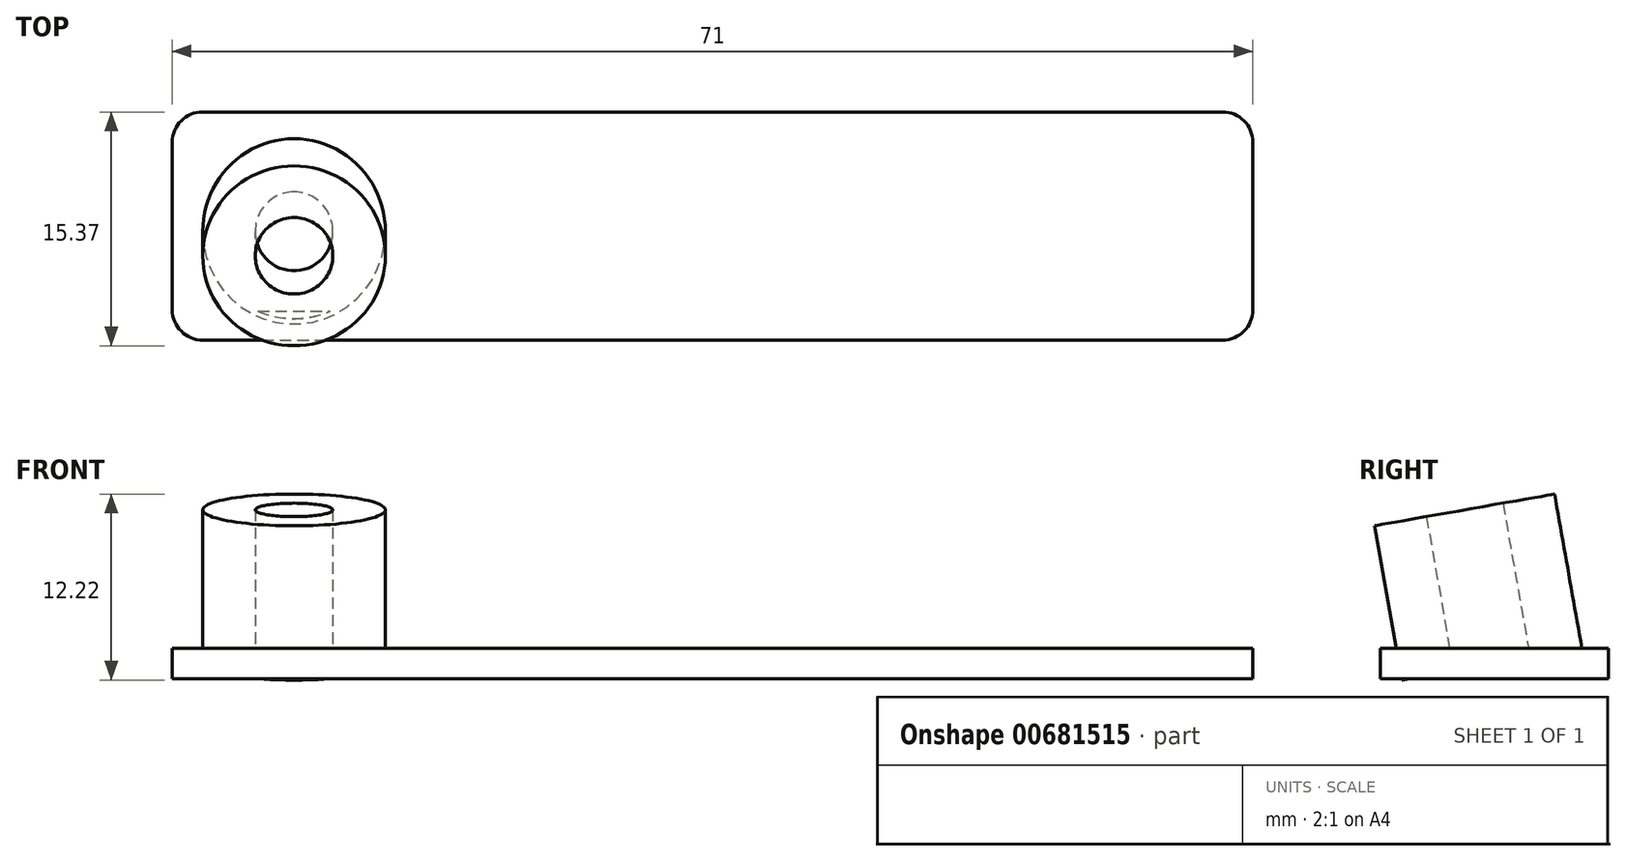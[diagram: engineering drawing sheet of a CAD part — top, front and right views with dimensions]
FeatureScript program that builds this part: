
annotation { "Feature Type Name" : "Feature", "Feature Type Description" : "" }
export const myFeature = defineFeature(function(context is Context, id is Id, definition is map)
    precondition{}
    {
        {
            var Q0;
            Q0=qCreatedBy(makeId("Top.planeOp"),FACE);
            var sketch = newSketch(context, id + "F0", { "sketchPlane" : qUnion([Q0])});
            skLineSegment(sketch, "E0.bottom", {"start": v(-35.5, 7.5) * mm, "end": v(35.5, 7.5) * mm});
            skLineSegment(sketch, "E0.top", {"start": v(-35.5, -7.5) * mm, "end": v(35.5, -7.5) * mm});
            skLineSegment(sketch, "E0.left", {"start": v(-35.5, 7.5) * mm, "end": v(-35.5, -7.5) * mm});
            skLineSegment(sketch, "E0.right", {"start": v(35.5, 7.5) * mm, "end": v(35.5, -7.5) * mm});
            skPoint(sketch, "E0.middle", {"position": v(0, 0) * mm});
            skSolve(sketch);
        }
        {
            var Q0;
            Q0 = qSketchRegion(id + "F0", true);
            extrude(context, id + "F1", {"entities" : qUnion([Q0]), "depth" : 2 * mm, "offsetDistance" : 25 * mm});
        }
        {
            var Q0;
            Q0=makeQuery(id+"F1.opExtrude","SWEPT_EDGE",EDGE,{"disambiguationData":[OSD([sQuery(id+"F0.wireOp",EDGE,"E0.bottom"),sQuery(id+"F0.wireOp",EDGE,"E0.left")])]});
            var Q1;
            Q1=makeQuery(id+"F1.opExtrude","SWEPT_EDGE",EDGE,{"disambiguationData":[OSD([sQuery(id+"F0.wireOp",EDGE,"E0.top"),sQuery(id+"F0.wireOp",EDGE,"E0.left")])]});
            var Q2;
            Q2=makeQuery(id+"F1.opExtrude","SWEPT_EDGE",EDGE,{"disambiguationData":[OSD([sQuery(id+"F0.wireOp",EDGE,"E0.top"),sQuery(id+"F0.wireOp",EDGE,"E0.right")])]});
            var Q3;
            Q3=makeQuery(id+"F1.opExtrude","SWEPT_EDGE",EDGE,{"disambiguationData":[OSD([sQuery(id+"F0.wireOp",EDGE,"E0.bottom"),sQuery(id+"F0.wireOp",EDGE,"E0.right")])]});
            fillet(context, id + "F2", {"entities" : qUnion([Q0, Q1, Q2, Q3]), "radius" : 2 * mm, "tangentPropagation" : true, "allowEdgeOverflow" : false});
        }
        {
            var Q0;
            Q0=makeQuery(id+"F1.opExtrude","CAP_EDGE",EDGE,{"disambiguationData":[OSD([sQuery(id+"F0.wireOp",EDGE,"E0.top")])],"isStart":false});
            cPlane(context, id + "F3", {"entities" : qUnion([Q0]), "cplaneType" : CPlaneType.LINE_ANGLE, "offset" : 25 * mm, "angle" : 100 * degree, "width" : 150 * mm, "height" : 150 * mm});
        }
        {
            var Q0;
            Q0=qCreatedBy(id+"F3.planeOp",FACE);
            var sketch = newSketch(context, id + "F4", { "sketchPlane" : qUnion([Q0])});
            skCircle(sketch, "E1", {"center": v(-27.5, 0) * mm, "radius": 6 * mm});
            skCircle(sketch, "E2", {"center": v(-27.5, 0) * mm, "radius": 2.55 * mm});
            skCircle(sketch, "E3.MirrorC", {"center": v(27.5, 0) * mm, "radius": 6 * mm});
            skCircle(sketch, "E4.MirrorC", {"center": v(27.5, 0) * mm, "radius": 2.55 * mm});
            skSolve(sketch);
        }
        {
            var Q0;
            Q0=makeQuery(id+"F4.imprint","IMPRINT",FACE,{"disambiguationData":[TD([[makeQuery(id+"F4.imprint","IMPRINT",EDGE,{"derivedFrom":sQuery(id+"F4.wireOp",EDGE,"E1")}),1.0]])]});
            var Q1;
            Q1=makeQuery(id+"F4.imprint","IMPRINT",FACE,{"disambiguationData":[TD([[makeQuery(id+"F4.imprint","IMPRINT",EDGE,{"derivedFrom":sQuery(id+"F4.wireOp",EDGE,"E3.MirrorC")}),-1.0]])]});
            extrude(context, id + "F5", {"entities" : qUnion([Q0, Q1]), "operationType" : NewBodyOperationType.ADD, "depth" : 8 * mm, "offsetDistance" : 25 * mm, "hasSecondDirection" : true, "secondDirectionOppositeDirection" : true, "secondDirectionDepth" : 2.3 * mm});
        }
    });
